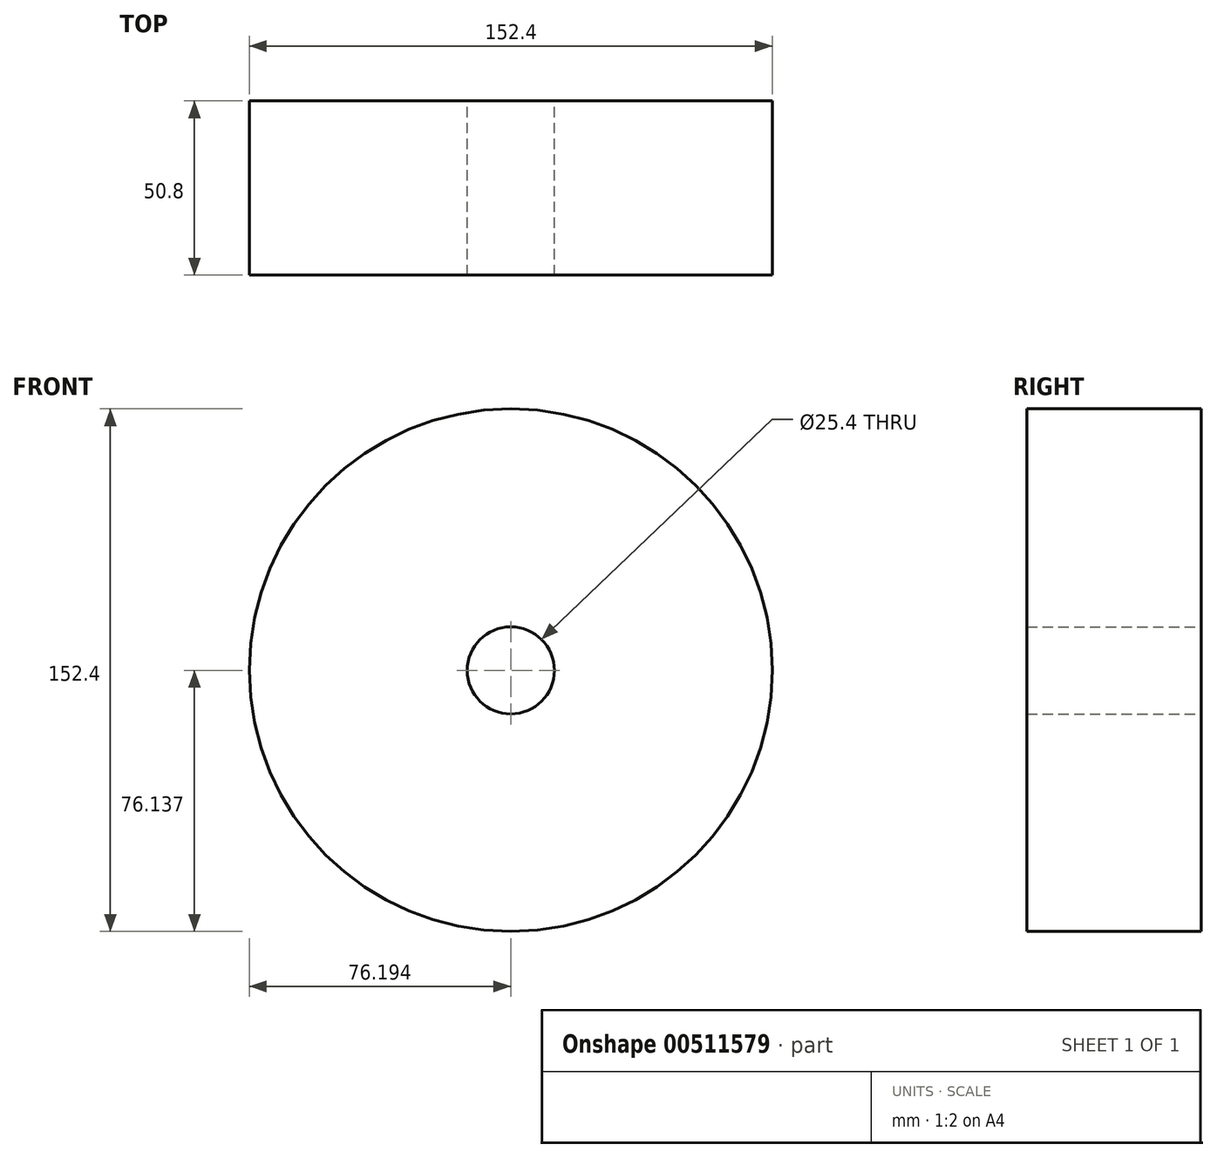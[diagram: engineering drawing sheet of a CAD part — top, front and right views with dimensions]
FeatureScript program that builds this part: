
annotation { "Feature Type Name" : "Feature", "Feature Type Description" : "" }
export const myFeature = defineFeature(function(context is Context, id is Id, definition is map)
    precondition{}
    {
        {
            var Q0;
            Q0=qCreatedBy(makeId("Front.planeOp"),FACE);
            var sketch = newSketch(context, id + "F0", { "sketchPlane" : qUnion([Q0])});
            skCircle(sketch, "E0", {"center": v(-27.49, 30.92) * mm, "radius": 76.2 * mm});
            skCircle(sketch, "E1", {"center": v(-27.5, 30.86) * mm, "radius": 12.7 * mm});
            skSolve(sketch);
        }
        {
            var Q0;
            Q0=makeQuery(id+"F0.imprint","IMPRINT",FACE,{"disambiguationData":[TD([[makeQuery(id+"F0.imprint","IMPRINT",EDGE,{"derivedFrom":sQuery(id+"F0.wireOp",EDGE,"E0")}),1.0]])]});
            extrude(context, id + "F1", {"entities" : qUnion([Q0]), "depth" : 50.8 * mm, "offsetDistance" : 25.4 * mm});
        }
    });
